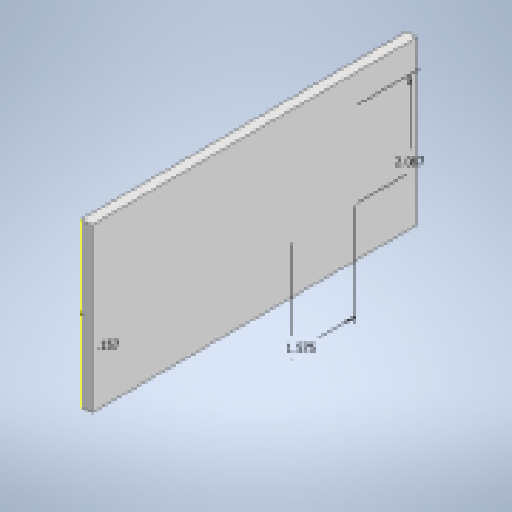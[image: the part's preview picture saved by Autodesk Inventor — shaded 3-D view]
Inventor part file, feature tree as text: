
AUTODESK INVENTOR PART (.ipt)
format: ipt  version: 2023 (Build 270158000, 158)  size: 145,920 bytes
history: native  units: in
note: dims shown in document units (in); Inventor stores cm internally (conversion verified against a paired STEP export)
features: extrude x2, sketch x2
ambient origin geometry x8: Origin, YZ Plane, XZ Plane, XY Plane, X Axis, Y Axis, Z Axis, Center Point
bodies: Solid1 (feature_tree)
feature tree (4):
  extrude  "Extrusion1"  Depth=4.0in
  extrude  "Extrusion2"  Depth=0.25in
  sketch  "Sketch1"  dims[d0=8.0in d1=4.0in]
  sketch  "Sketch2"  dims[d2=0.25in d3=0.0in d4=0.1575in d5=2.0866in d6=1.5748in d7=0.3504in d8=0.3504in d9=0.25in d10=0.0in]
